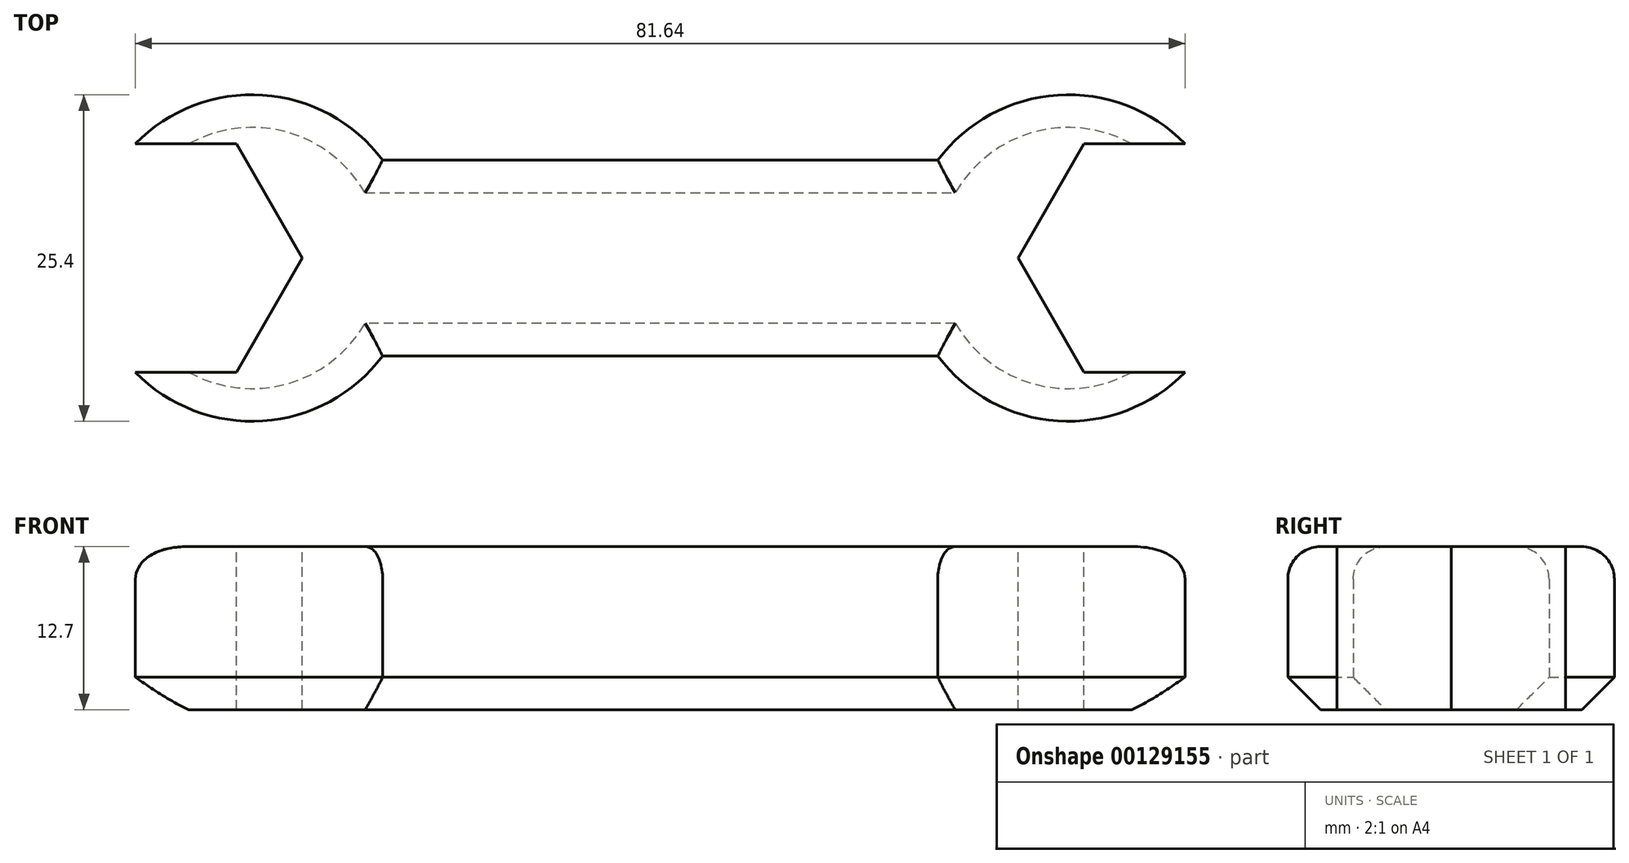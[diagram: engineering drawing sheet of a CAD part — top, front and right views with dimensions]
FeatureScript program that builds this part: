
annotation { "Feature Type Name" : "Feature", "Feature Type Description" : "" }
export const myFeature = defineFeature(function(context is Context, id is Id, definition is map)
    precondition{}
    {
        {
            var Q0;
            Q0=qCreatedBy(makeId("Top.planeOp"),FACE);
            var sketch = newSketch(context, id + "F0", { "sketchPlane" : qUnion([Q0])});
            skArc(sketch, "E0", {"start": v(-21.59, 7.62) * mm, "mid": v(-44.45, 0) * mm, "end": v(-21.6, -7.62) * mm});
            skArc(sketch, "E1", {"start": v(21.6, -7.62) * mm, "mid": v(44.45, 0) * mm, "end": v(21.59, 7.62) * mm});
            skLineSegment(sketch, "E2", {"start": v(-21.59, 7.62) * mm, "end": v(21.59, 7.62) * mm});
            skLineSegment(sketch, "E3", {"start": v(-21.59, -7.62) * mm, "end": v(21.59, -7.62) * mm});
            skLineSegment(sketch, "E4", {"start": v(-31.75, 0) * mm, "end": v(31.75, 0) * mm, "construction": true});
            skSolve(sketch);
        }
        {
            var Q0;
            Q0 = qSketchRegion(id + "F0", true);
            extrude(context, id + "F1", {"entities" : qUnion([Q0]), "endBound" : BoundingType.SYMMETRIC, "depth" : 12.7 * mm});
        }
        {
            var Q0;
            Q0=makeQuery(id+"F1.opExtrude","CAP_FACE",FACE,{"disambiguationData":[OSD([sQuery(id+"F0.wireOp",EDGE,"E0"),sQuery(id+"F0.wireOp",EDGE,"E1"),sQuery(id+"F0.wireOp",EDGE,"E2"),sQuery(id+"F0.wireOp",EDGE,"E3")])],"isStart":false});
            var sketch = newSketch(context, id + "F2", { "sketchPlane" : qUnion([Q0])});
            skCircle(sketch, "E5.cCircle", {"center": v(-38.1, 0) * mm, "radius": 8.9 * mm, "construction": true});
            skLineSegment(sketch, "E5.0", {"start": v(-48.37, 0) * mm, "end": v(-43.23, 8.89) * mm});
            skLineSegment(sketch, "E5.1", {"start": v(-43.23, 8.89) * mm, "end": v(-32.97, 8.9) * mm});
            skLineSegment(sketch, "E5.2", {"start": v(-32.97, 8.89) * mm, "end": v(-27.83, 0) * mm});
            skLineSegment(sketch, "E5.3", {"start": v(-27.83, 0) * mm, "end": v(-32.97, -8.9) * mm});
            skLineSegment(sketch, "E5.4", {"start": v(-32.97, -8.89) * mm, "end": v(-43.23, -8.9) * mm});
            skLineSegment(sketch, "E5.5", {"start": v(-43.23, -8.89) * mm, "end": v(-48.37, 0) * mm});
            skPoint(sketch, "E5.0.midPoint", {"position": v(-45.8, 4.44) * mm});
            skPoint(sketch, "E6", {"position": v(-44.45, 0) * mm});
            skSolve(sketch);
        }
        {
            var Q0;
            Q0 = qSketchRegion(id + "F2", true);
            extrude(context, id + "F3", {"entities" : qUnion([Q0]), "endBound" : BoundingType.THROUGH_ALL, "oppositeDirection" : true, "depth" : 25.4 * mm});
        }
        {
            var Q0;
            Q0=makeQuery(id+"F3.opExtrude","SWEPT_BODY",BODY,{"disambiguationData":[OSD([sQuery(id+"F2.wireOp",EDGE,"E5.0"),sQuery(id+"F2.wireOp",EDGE,"E5.1"),sQuery(id+"F2.wireOp",EDGE,"E5.2"),sQuery(id+"F2.wireOp",EDGE,"E5.3"),sQuery(id+"F2.wireOp",EDGE,"E5.4"),sQuery(id+"F2.wireOp",EDGE,"E5.5")])]});
            var Q1;
            Q1=qCreatedBy(makeId("Right.planeOp"),FACE);
            mirror(context, id + "F4", {"operationType" : NewBodyOperationType.REMOVE, "entities" : qUnion([Q0]), "mirrorPlane" : qUnion([Q1])});
        }
        {
            var Q0;
            Q0=makeQuery(id+"F3.opExtrude","SWEPT_BODY",BODY,{"disambiguationData":[OSD([sQuery(id+"F2.wireOp",EDGE,"E5.0"),sQuery(id+"F2.wireOp",EDGE,"E5.1"),sQuery(id+"F2.wireOp",EDGE,"E5.2"),sQuery(id+"F2.wireOp",EDGE,"E5.3"),sQuery(id+"F2.wireOp",EDGE,"E5.4"),sQuery(id+"F2.wireOp",EDGE,"E5.5")])]});
            var Q1;
            Q1=makeQuery(id+"F1.opExtrude","SWEPT_BODY",BODY,{"disambiguationData":[OSD([sQuery(id+"F0.wireOp",EDGE,"E0"),sQuery(id+"F0.wireOp",EDGE,"E1"),sQuery(id+"F0.wireOp",EDGE,"E2"),sQuery(id+"F0.wireOp",EDGE,"E3")])]});
            booleanBodies(context, id + "F5", {"operationType" : BooleanOperationType.SUBTRACTION, "tools" : qUnion([Q0]), "targets" : qUnion([Q1])});
        }
        {
            var Q0;
            Q0=makeQuery(id+"F1.opExtrude","CAP_EDGE",EDGE,{"disambiguationData":[OSD([sQuery(id+"F0.wireOp",EDGE,"E3")])],"isStart":false});
            var Q1;
            {var subQ0=sQuery(id+"F0.wireOp",EDGE,"E0");var subQ1=sQuery(id+"F0.wireOp",EDGE,"E3");Q1=makeQuery(id+"F5.opBoolean","SPLIT",EDGE,{"disambiguationData":[TD([makeQuery(id+"F1.opExtrude","SWEPT_FACE",FACE,{"disambiguationData":[OSD([subQ1])]})])],"derivedFrom":makeQuery(id+"F1.opExtrude","CAP_EDGE",EDGE,{"disambiguationData":[OSD([subQ0])],"isStart":false})});}
            var Q2;
            {var subQ0=sQuery(id+"F0.wireOp",EDGE,"E3");var subQ1=sQuery(id+"F0.wireOp",EDGE,"E1");Q2=makeQuery(id+"F4.boolean.opBoolean","SPLIT",EDGE,{"disambiguationData":[TD([makeQuery(id+"F1.opExtrude","SWEPT_FACE",FACE,{"disambiguationData":[OSD([subQ0])]})])],"derivedFrom":makeQuery(id+"F1.opExtrude","CAP_EDGE",EDGE,{"disambiguationData":[OSD([subQ1])],"isStart":false})});}
            var Q3;
            {var subQ0=sQuery(id+"F0.wireOp",EDGE,"E2");var subQ1=sQuery(id+"F0.wireOp",EDGE,"E1");Q3=makeQuery(id+"F4.boolean.opBoolean","SPLIT",EDGE,{"disambiguationData":[TD([makeQuery(id+"F1.opExtrude","SWEPT_FACE",FACE,{"disambiguationData":[OSD([subQ0])]})])],"derivedFrom":makeQuery(id+"F1.opExtrude","CAP_EDGE",EDGE,{"disambiguationData":[OSD([subQ1])],"isStart":false})});}
            var Q4;
            Q4=makeQuery(id+"F1.opExtrude","CAP_EDGE",EDGE,{"disambiguationData":[OSD([sQuery(id+"F0.wireOp",EDGE,"E2")])],"isStart":false});
            var Q5;
            {var subQ0=sQuery(id+"F0.wireOp",EDGE,"E0");var subQ1=sQuery(id+"F0.wireOp",EDGE,"E2");Q5=makeQuery(id+"F5.opBoolean","SPLIT",EDGE,{"disambiguationData":[TD([makeQuery(id+"F1.opExtrude","SWEPT_FACE",FACE,{"disambiguationData":[OSD([subQ1])]})])],"derivedFrom":makeQuery(id+"F1.opExtrude","CAP_EDGE",EDGE,{"disambiguationData":[OSD([subQ0])],"isStart":false})});}
            fillet(context, id + "F6", {"entities" : qUnion([Q0, Q1, Q2, Q3, Q4, Q5]), "radius" : 2.54 * mm, "tangentPropagation" : true, "allowEdgeOverflow" : false});
        }
        {
            var Q0;
            {var subQ0=sQuery(id+"F0.wireOp",EDGE,"E0");var subQ1=sQuery(id+"F0.wireOp",EDGE,"E3");Q0=makeQuery(id+"F5.opBoolean","SPLIT",EDGE,{"disambiguationData":[TD([makeQuery(id+"F1.opExtrude","SWEPT_FACE",FACE,{"disambiguationData":[OSD([subQ1])]})])],"derivedFrom":makeQuery(id+"F1.opExtrude","CAP_EDGE",EDGE,{"disambiguationData":[OSD([subQ0])],"isStart":true})});}
            var Q1;
            Q1=makeQuery(id+"F1.opExtrude","CAP_EDGE",EDGE,{"disambiguationData":[OSD([sQuery(id+"F0.wireOp",EDGE,"E3")])],"isStart":true});
            var Q2;
            {var subQ0=sQuery(id+"F0.wireOp",EDGE,"E3");var subQ1=sQuery(id+"F0.wireOp",EDGE,"E1");Q2=makeQuery(id+"F4.boolean.opBoolean","SPLIT",EDGE,{"disambiguationData":[TD([makeQuery(id+"F1.opExtrude","SWEPT_FACE",FACE,{"disambiguationData":[OSD([subQ0])]})])],"derivedFrom":makeQuery(id+"F1.opExtrude","CAP_EDGE",EDGE,{"disambiguationData":[OSD([subQ1])],"isStart":true})});}
            var Q3;
            {var subQ0=sQuery(id+"F0.wireOp",EDGE,"E2");var subQ1=sQuery(id+"F0.wireOp",EDGE,"E1");Q3=makeQuery(id+"F4.boolean.opBoolean","SPLIT",EDGE,{"disambiguationData":[TD([makeQuery(id+"F1.opExtrude","SWEPT_FACE",FACE,{"disambiguationData":[OSD([subQ0])]})])],"derivedFrom":makeQuery(id+"F1.opExtrude","CAP_EDGE",EDGE,{"disambiguationData":[OSD([subQ1])],"isStart":true})});}
            var Q4;
            {var subQ0=sQuery(id+"F0.wireOp",EDGE,"E0");var subQ1=sQuery(id+"F0.wireOp",EDGE,"E2");Q4=makeQuery(id+"F5.opBoolean","SPLIT",EDGE,{"disambiguationData":[TD([makeQuery(id+"F1.opExtrude","SWEPT_FACE",FACE,{"disambiguationData":[OSD([subQ1])]})])],"derivedFrom":makeQuery(id+"F1.opExtrude","CAP_EDGE",EDGE,{"disambiguationData":[OSD([subQ0])],"isStart":true})});}
            var Q5;
            Q5=makeQuery(id+"F1.opExtrude","CAP_EDGE",EDGE,{"disambiguationData":[OSD([sQuery(id+"F0.wireOp",EDGE,"E2")])],"isStart":true});
            chamfer(context, id + "F7", {"entities" : qUnion([Q0, Q1, Q2, Q3, Q4, Q5]), "width" : 2.54 * mm, "tangentPropagation" : true});
        }
    });
